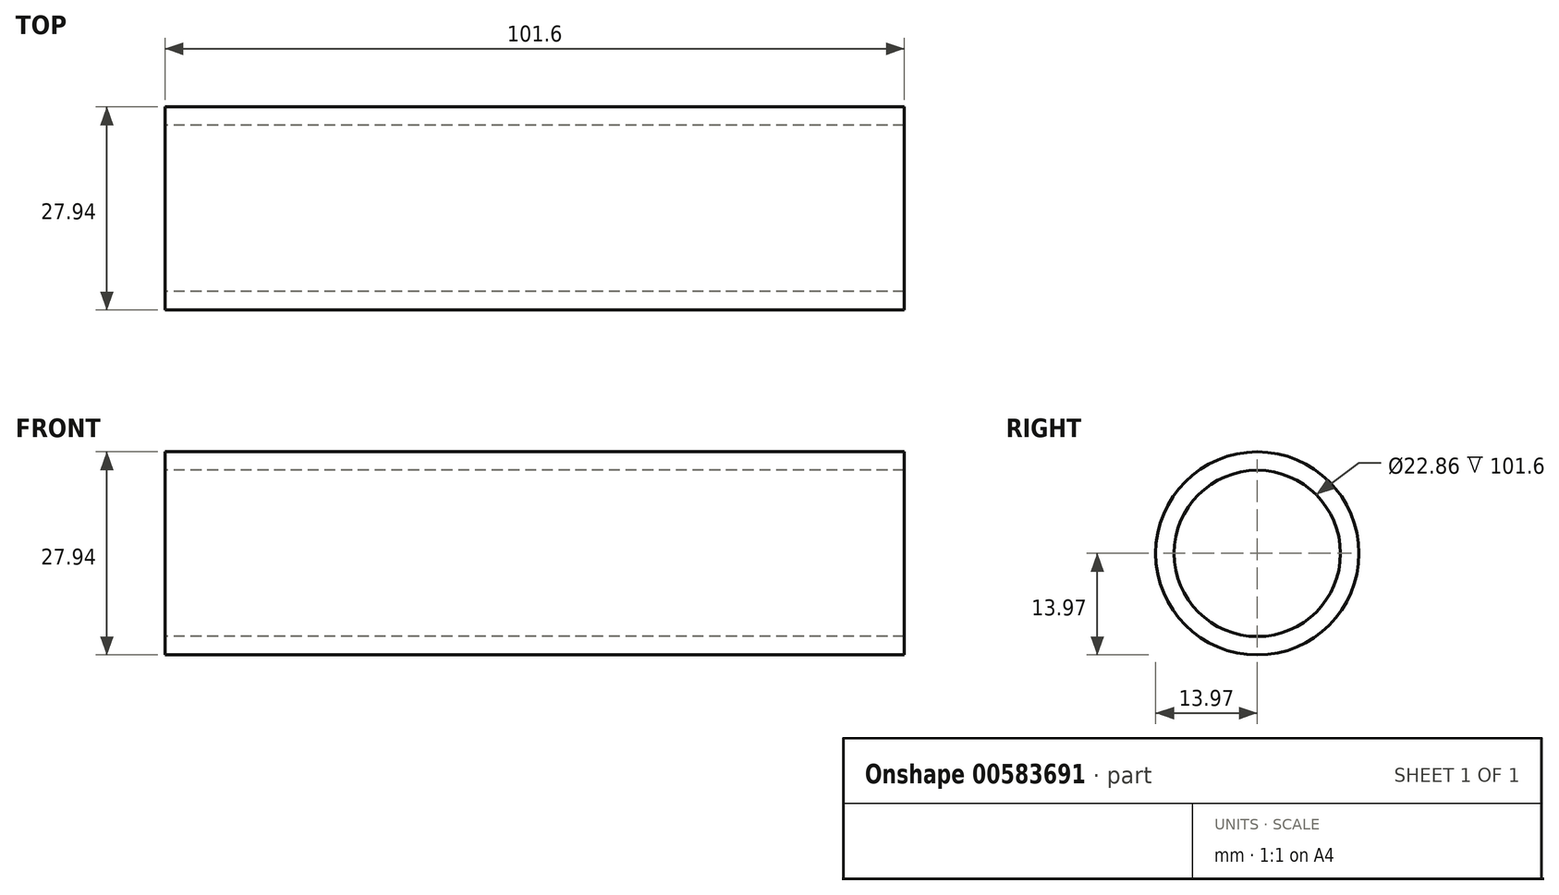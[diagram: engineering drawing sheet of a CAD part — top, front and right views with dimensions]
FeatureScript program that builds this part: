
annotation { "Feature Type Name" : "Feature", "Feature Type Description" : "" }
export const myFeature = defineFeature(function(context is Context, id is Id, definition is map)
    precondition{}
    {
        {
            var Q0;
            Q0=qCreatedBy(makeId("Right.planeOp"),FACE);
            var sketch = newSketch(context, id + "F0", { "sketchPlane" : qUnion([Q0])});
            skCircle(sketch, "E0", {"center": v(0, 0) * mm, "radius": 11.43 * mm});
            skCircle(sketch, "E1.0", {"center": v(0, 0) * mm, "radius": 13.97 * mm});
            skSolve(sketch);
        }
        {
            var Q0;
            Q0 = qSketchRegion(id + "F0", true);
            extrude(context, id + "F1", {"entities" : qUnion([Q0]), "depth" : 101.6 * mm, "offsetDistance" : 25.4 * mm});
        }
    });
